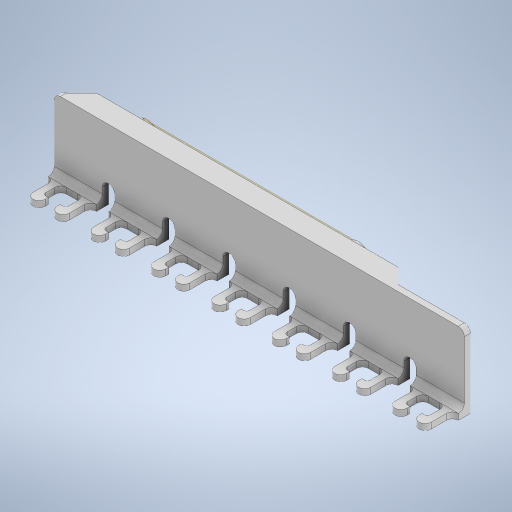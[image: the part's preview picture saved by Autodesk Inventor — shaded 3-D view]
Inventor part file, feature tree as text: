
AUTODESK INVENTOR PART (.ipt)
format: ipt  version: 2024.3 (Build 283343000, 343)  size: 651,776 bytes
history: native  units: in
note: dims shown in document units (in); Inventor stores cm internally (conversion verified against a paired STEP export)
features: reference x15, other x11, extrude x7, sketch x7, fillet x4, plane x1, chamfer x1, projected_geometry x1
ambient origin geometry x8: Origin, YZ Plane, XZ Plane, XY Plane, X Axis, Y Axis, Z Axis, Center Point
bodies: Solid1 (feature_tree)
feature tree (47):
  plane  "Work Plane1"
  extrude  "Extrusion1"  Depth=0.1969in TaperAngle=0.0deg
  extrude  "Extrusion2"  Depth=0.1378in
  extrude  "Extrusion3"  Depth=0.0787in TaperAngle=0.0deg
  extrude  "Extrusion4"  Depth=0.0787in
  fillet  "Fillet1"  Radius=0.0787in
  fillet  "Fillet2"  Radius=0.0394in
  extrude  "Extrusion6"  Depth=0.1575in
  extrude  "Extrusion7"  Depth=0.2362in
  extrude  "Extrusion9"  Depth=0.0866in
  fillet  "Fillet4"  Radius=0.0787in
  fillet  "Fillet5"  Radius=0.0787in
  chamfer  "Chamfer3"  Distance=0.0787in
  sketch  "Sketch1"  dims[d0=3.937in d1=0.1969in d2=0.0in]
  reference  "Reference1"
  reference  "Reference2"
  sketch  "Sketch2"  dims[d3=0.1378in d4=0.1378in]
  reference  "Reference3"
  reference  "Reference4"
  sketch  "Sketch3"  dims[d5=0.9843in d6=0.0787in d7=0.0in]
  reference  "Reference5"
  reference  "Reference6"
  reference  "Reference7"
  reference  "Reference8"
  reference  "Reference9"
  reference  "Reference10"
  reference  "Reference11"
  sketch  "Sketch4"  dims[d8=0.6299in d9=0.0787in]
  sketch  "Sketch6"  dims[d10=2.7559in d12=0.7874in d13=0.3937in d15=0.3937in d17=0.0787in d18=0.0in d19=0.0394in]
  reference  "Reference12"
  projected_geometry  "Projected Loop1"
  reference  "Reference13"
  sketch  "Sketch7"  dims[d20=0.0787in d21=0.1575in]
  reference  "Reference14"
  reference  "Reference15"
  sketch  "Sketch9"  dims[d22=0.3543in d23=0.2362in d24=0.0866in d32=0.0787in d33=0.0in d43=0.0787in d44=0.0787in d51=0.1575in d52=0.0079in d53=0.0709in d54=0.0in d55=0.2756in d56=0.0in d60=2.3622in d62=0.7874in d63=0.3937in d65=0.3937in d67=0.0787in d68=0.0in d69=0.0787in d70=0.0787in d71=0.0787in d72=2.7559in d74=0.7874in d75=0.3937in d77=0.3937in d79=0.0787in d80=0.1969in d81=0.0787in d82=45.0deg d83=0.315in]
  other  "<userpath>\Dropbox\elec\Mechanical\DCBuddyV2\PCB\_TOP_Design.iam"
  other  "_TOP_Design.iam"
  other  "DCB2_Flange:1"
  other  "dcbuddy_v2:1"
  other  "CUI-PJ-002A_V_CMP-167-0003-2:8"
  other  "CUI-PJ-002A_V_CMP-167-0003-2:2"
  other  "CUI-PJ-002A_V_CMP-167-0003-2:7"
  other  "CUI-PJ-002A_V_CMP-167-0003-2:6"
  other  "CUI-PJ-002A_V_CMP-167-0003-2:5"
  other  "CUI-PJ-002A_V_CMP-167-0003-2:4"
  other  "CUI-PJ-002A_V_CMP-167-0003-2:3"
